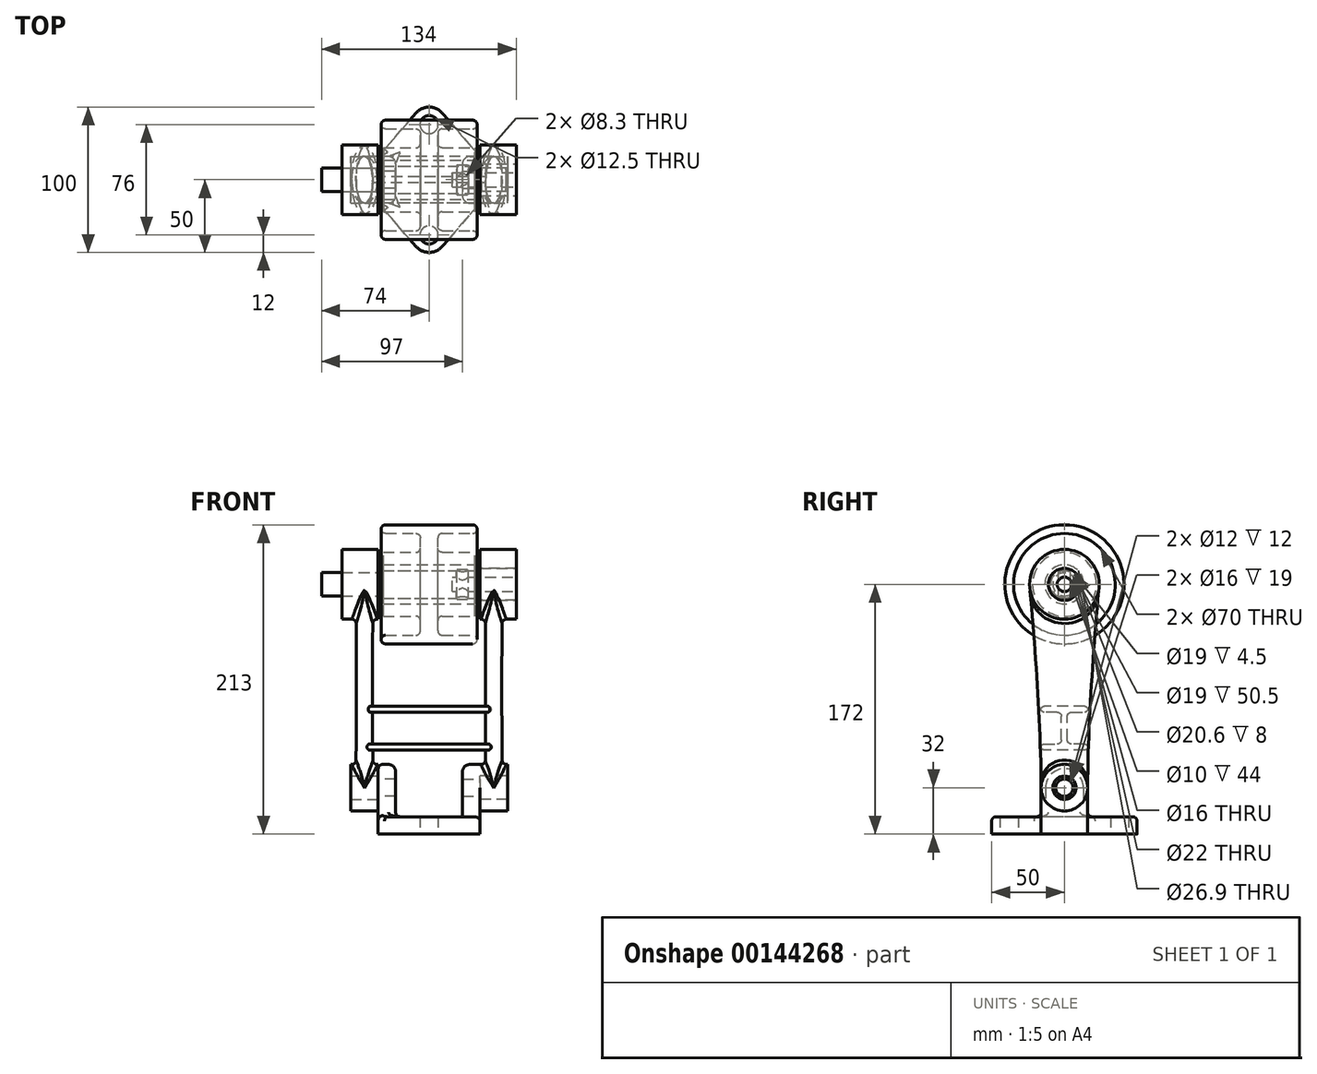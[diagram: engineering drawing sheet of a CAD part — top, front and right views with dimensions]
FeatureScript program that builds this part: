
annotation { "Feature Type Name" : "Feature", "Feature Type Description" : "" }
export const myFeature = defineFeature(function(context is Context, id is Id, definition is map)
    precondition{}
    {
        {
            var Q0;
            Q0=qCreatedBy(makeId("Top.planeOp"),FACE);
            var sketch = newSketch(context, id + "F0", { "sketchPlane" : qUnion([Q0])});
            skLineSegment(sketch, "E0", {"start": v(-9.06, -45.87) * mm, "end": v(-35, -16) * mm});
            skLineSegment(sketch, "E1", {"start": v(-35, 16) * mm, "end": v(-9.06, 45.87) * mm});
            skLineSegment(sketch, "E2", {"start": v(9.06, 45.87) * mm, "end": v(35, 16) * mm});
            skLineSegment(sketch, "E3", {"start": v(35, -16) * mm, "end": v(9.06, -45.87) * mm});
            skLineSegment(sketch, "E4", {"start": v(35, -16) * mm, "end": v(35, 16) * mm});
            skLineSegment(sketch, "E5", {"start": v(-35, -16) * mm, "end": v(-35, 16) * mm});
            skPoint(sketch, "E6.orphan", {"position": v(-48.9, 0) * mm});
            skPoint(sketch, "E7.orphan", {"position": v(48.9, 0) * mm});
            skPoint(sketch, "E8.visualSharp", {"position": v(0, -56.3) * mm});
            skArc(sketch, "E8.filletArc", {"start": v(-9.06, -45.87) * mm, "mid": v(0, -50) * mm, "end": v(9.06, -45.87) * mm});
            skPoint(sketch, "E9.visualSharp", {"position": v(0, 56.3) * mm});
            skArc(sketch, "E9.filletArc", {"start": v(9.06, 45.87) * mm, "mid": v(0, 50) * mm, "end": v(-9.06, 45.87) * mm});
            skCircle(sketch, "E10", {"center": v(0, -38) * mm, "radius": 6.25 * mm});
            skCircle(sketch, "E11", {"center": v(0, 38) * mm, "radius": 6.25 * mm});
            skSolve(sketch);
        }
        {
            var Q0;
            Q0 = qSketchRegion(id + "F0", true);
            extrude(context, id + "F1", {"entities" : qUnion([Q0]), "depth" : 12 * mm});
        }
        {
            var Q0;
            Q0=makeQuery(id+"F1.opExtrude","SWEPT_FACE",FACE,{"disambiguationData":[OSD([sQuery(id+"F0.wireOp",EDGE,"E5")])]});
            var sketch = newSketch(context, id + "F2", { "sketchPlane" : qUnion([Q0])});
            skLineSegment(sketch, "E12", {"start": v(-16, 0) * mm, "end": v(-16, 32) * mm});
            skLineSegment(sketch, "E13", {"start": v(16, 0) * mm, "end": v(16, 32) * mm});
            skArc(sketch, "E14", {"start": v(16, 32) * mm, "mid": v(0, 48) * mm, "end": v(-16, 32) * mm});
            skLineSegment(sketch, "E15", {"start": v(-16, 0) * mm, "end": v(16, 0) * mm});
            skCircle(sketch, "E16", {"center": v(0, 32) * mm, "radius": 6 * mm});
            skSolve(sketch);
        }
        {
            var Q0;
            Q0 = qSketchRegion(id + "F2", true);
            extrude(context, id + "F3", {"entities" : qUnion([Q0]), "operationType" : NewBodyOperationType.ADD, "oppositeDirection" : true, "depth" : 12 * mm});
        }
        {
            var Q0;
            Q0=makeQuery(id+"F1.opExtrude","SWEPT_BODY",BODY,{"disambiguationData":[OSD([sQuery(id+"F0.wireOp",EDGE,"E0"),sQuery(id+"F0.wireOp",EDGE,"E1"),sQuery(id+"F0.wireOp",EDGE,"E2"),sQuery(id+"F0.wireOp",EDGE,"E3"),sQuery(id+"F0.wireOp",EDGE,"E4"),sQuery(id+"F0.wireOp",EDGE,"E5"),sQuery(id+"F0.wireOp",EDGE,"E8.filletArc"),sQuery(id+"F0.wireOp",EDGE,"E9.filletArc"),sQuery(id+"F0.wireOp",EDGE,"E10"),sQuery(id+"F0.wireOp",EDGE,"E11")])]});
            var Q1;
            Q1=qCreatedBy(makeId("Right.planeOp"),FACE);
            mirror(context, id + "F4", {"operationType" : NewBodyOperationType.ADD, "entities" : qUnion([Q0]), "mirrorPlane" : qUnion([Q1])});
        }
        {
            var Q0;
            Q0=makeQuery(id+"F4.opPattern","COPY",EDGE,{"derivedFrom":makeQuery(id+"F3.boolean.opBoolean","INTERSECT",EDGE,{"derivedFrom":[makeQuery(id+"F1.opExtrude","CAP_FACE",FACE,{"disambiguationData":[OSD([sQuery(id+"F0.wireOp",EDGE,"E0"),sQuery(id+"F0.wireOp",EDGE,"E1"),sQuery(id+"F0.wireOp",EDGE,"E2"),sQuery(id+"F0.wireOp",EDGE,"E3"),sQuery(id+"F0.wireOp",EDGE,"E4"),sQuery(id+"F0.wireOp",EDGE,"E5"),sQuery(id+"F0.wireOp",EDGE,"E8.filletArc"),sQuery(id+"F0.wireOp",EDGE,"E9.filletArc"),sQuery(id+"F0.wireOp",EDGE,"E10"),sQuery(id+"F0.wireOp",EDGE,"E11")])],"isStart":false}),makeQuery(id+"F3.opExtrude","SWEPT_FACE",FACE,{"disambiguationData":[OSD([sQuery(id+"F2.wireOp",EDGE,"E12")])]})]}),"instanceName":"1"});
            var Q1;
            Q1=makeQuery(id+"F4.opPattern","COPY",EDGE,{"derivedFrom":makeQuery(id+"F3.boolean.opBoolean","INTERSECT",EDGE,{"derivedFrom":[makeQuery(id+"F1.opExtrude","CAP_FACE",FACE,{"disambiguationData":[OSD([sQuery(id+"F0.wireOp",EDGE,"E0"),sQuery(id+"F0.wireOp",EDGE,"E1"),sQuery(id+"F0.wireOp",EDGE,"E2"),sQuery(id+"F0.wireOp",EDGE,"E3"),sQuery(id+"F0.wireOp",EDGE,"E4"),sQuery(id+"F0.wireOp",EDGE,"E5"),sQuery(id+"F0.wireOp",EDGE,"E8.filletArc"),sQuery(id+"F0.wireOp",EDGE,"E9.filletArc"),sQuery(id+"F0.wireOp",EDGE,"E10"),sQuery(id+"F0.wireOp",EDGE,"E11")])],"isStart":false}),makeQuery(id+"F3.opExtrude","CAP_FACE",FACE,{"disambiguationData":[OSD([sQuery(id+"F2.wireOp",EDGE,"E12"),sQuery(id+"F2.wireOp",EDGE,"E13"),sQuery(id+"F2.wireOp",EDGE,"E14"),sQuery(id+"F2.wireOp",EDGE,"E15"),sQuery(id+"F2.wireOp",EDGE,"E16")])],"isStart":false})]}),"instanceName":"1"});
            var Q2;
            Q2=makeQuery(id+"F4.opPattern","COPY",EDGE,{"derivedFrom":makeQuery(id+"F3.boolean.opBoolean","INTERSECT",EDGE,{"derivedFrom":[makeQuery(id+"F1.opExtrude","CAP_FACE",FACE,{"disambiguationData":[OSD([sQuery(id+"F0.wireOp",EDGE,"E0"),sQuery(id+"F0.wireOp",EDGE,"E1"),sQuery(id+"F0.wireOp",EDGE,"E2"),sQuery(id+"F0.wireOp",EDGE,"E3"),sQuery(id+"F0.wireOp",EDGE,"E4"),sQuery(id+"F0.wireOp",EDGE,"E5"),sQuery(id+"F0.wireOp",EDGE,"E8.filletArc"),sQuery(id+"F0.wireOp",EDGE,"E9.filletArc"),sQuery(id+"F0.wireOp",EDGE,"E10"),sQuery(id+"F0.wireOp",EDGE,"E11")])],"isStart":false}),makeQuery(id+"F3.opExtrude","SWEPT_FACE",FACE,{"disambiguationData":[OSD([sQuery(id+"F2.wireOp",EDGE,"E13")])]})]}),"instanceName":"1"});
            var Q3;
            Q3=makeQuery(id+"F3.boolean.opBoolean","INTERSECT",EDGE,{"derivedFrom":[makeQuery(id+"F1.opExtrude","CAP_FACE",FACE,{"disambiguationData":[OSD([sQuery(id+"F0.wireOp",EDGE,"E0"),sQuery(id+"F0.wireOp",EDGE,"E1"),sQuery(id+"F0.wireOp",EDGE,"E2"),sQuery(id+"F0.wireOp",EDGE,"E3"),sQuery(id+"F0.wireOp",EDGE,"E4"),sQuery(id+"F0.wireOp",EDGE,"E5"),sQuery(id+"F0.wireOp",EDGE,"E8.filletArc"),sQuery(id+"F0.wireOp",EDGE,"E9.filletArc"),sQuery(id+"F0.wireOp",EDGE,"E10"),sQuery(id+"F0.wireOp",EDGE,"E11")])],"isStart":false}),makeQuery(id+"F3.opExtrude","SWEPT_FACE",FACE,{"disambiguationData":[OSD([sQuery(id+"F2.wireOp",EDGE,"E13")])]})]});
            var Q4;
            Q4=makeQuery(id+"F3.boolean.opBoolean","INTERSECT",EDGE,{"derivedFrom":[makeQuery(id+"F1.opExtrude","CAP_FACE",FACE,{"disambiguationData":[OSD([sQuery(id+"F0.wireOp",EDGE,"E0"),sQuery(id+"F0.wireOp",EDGE,"E1"),sQuery(id+"F0.wireOp",EDGE,"E2"),sQuery(id+"F0.wireOp",EDGE,"E3"),sQuery(id+"F0.wireOp",EDGE,"E4"),sQuery(id+"F0.wireOp",EDGE,"E5"),sQuery(id+"F0.wireOp",EDGE,"E8.filletArc"),sQuery(id+"F0.wireOp",EDGE,"E9.filletArc"),sQuery(id+"F0.wireOp",EDGE,"E10"),sQuery(id+"F0.wireOp",EDGE,"E11")])],"isStart":false}),makeQuery(id+"F3.opExtrude","CAP_FACE",FACE,{"disambiguationData":[OSD([sQuery(id+"F2.wireOp",EDGE,"E12"),sQuery(id+"F2.wireOp",EDGE,"E13"),sQuery(id+"F2.wireOp",EDGE,"E14"),sQuery(id+"F2.wireOp",EDGE,"E15"),sQuery(id+"F2.wireOp",EDGE,"E16")])],"isStart":false})]});
            var Q5;
            Q5=makeQuery(id+"F3.boolean.opBoolean","INTERSECT",EDGE,{"derivedFrom":[makeQuery(id+"F1.opExtrude","CAP_FACE",FACE,{"disambiguationData":[OSD([sQuery(id+"F0.wireOp",EDGE,"E0"),sQuery(id+"F0.wireOp",EDGE,"E1"),sQuery(id+"F0.wireOp",EDGE,"E2"),sQuery(id+"F0.wireOp",EDGE,"E3"),sQuery(id+"F0.wireOp",EDGE,"E4"),sQuery(id+"F0.wireOp",EDGE,"E5"),sQuery(id+"F0.wireOp",EDGE,"E8.filletArc"),sQuery(id+"F0.wireOp",EDGE,"E9.filletArc"),sQuery(id+"F0.wireOp",EDGE,"E10"),sQuery(id+"F0.wireOp",EDGE,"E11")])],"isStart":false}),makeQuery(id+"F3.opExtrude","SWEPT_FACE",FACE,{"disambiguationData":[OSD([sQuery(id+"F2.wireOp",EDGE,"E12")])]})]});
            fillet(context, id + "F5", {"entities" : qUnion([Q0, Q1, Q2, Q3, Q4, Q5]), "radius" : 3 * mm, "tangentPropagation" : true, "allowEdgeOverflow" : false});
        }
        {
            var Q0;
            Q0=makeQuery(id+"F1.opExtrude","CAP_EDGE",EDGE,{"disambiguationData":[OSD([sQuery(id+"F0.wireOp",EDGE,"E1")])],"isStart":false});
            var Q1;
            Q1=makeQuery(id+"F1.opExtrude","CAP_EDGE",EDGE,{"disambiguationData":[OSD([sQuery(id+"F0.wireOp",EDGE,"E0")])],"isStart":false});
            fillet(context, id + "F6", {"entities" : qUnion([Q0, Q1]), "radius" : 3 * mm, "tangentPropagation" : true, "allowEdgeOverflow" : false});
        }
        {
            var Q0;
            Q0=makeQuery(id+"F4.opPattern","COPY",EDGE,{"derivedFrom":makeQuery(id+"F3.opExtrude","CAP_EDGE",EDGE,{"disambiguationData":[OSD([sQuery(id+"F2.wireOp",EDGE,"E14")])],"isStart":false}),"instanceName":"1"});
            var Q1;
            Q1=makeQuery(id+"F3.opExtrude","CAP_EDGE",EDGE,{"disambiguationData":[OSD([sQuery(id+"F2.wireOp",EDGE,"E14")])],"isStart":false});
            fillet(context, id + "F7", {"entities" : qUnion([Q0, Q1]), "radius" : 5 * mm, "tangentPropagation" : true, "allowEdgeOverflow" : false});
        }
        {
            var Q0;
            Q0=makeQuery(id+"F4.boolean.opBoolean","MERGE",FACE,{"derivedFrom":[makeQuery(id+"F1.opExtrude","SWEPT_FACE",FACE,{"disambiguationData":[OSD([sQuery(id+"F0.wireOp",EDGE,"E4")])]}),makeQuery(id+"F4.opPattern","COPY",FACE,{"derivedFrom":makeQuery(id+"F3.boolean.opBoolean","MERGE",FACE,{"derivedFrom":[makeQuery(id+"F1.opExtrude","SWEPT_FACE",FACE,{"disambiguationData":[OSD([sQuery(id+"F0.wireOp",EDGE,"E5")])]}),makeQuery(id+"F3.opExtrude","CAP_FACE",FACE,{"disambiguationData":[OSD([sQuery(id+"F2.wireOp",EDGE,"E12"),sQuery(id+"F2.wireOp",EDGE,"E13"),sQuery(id+"F2.wireOp",EDGE,"E14"),sQuery(id+"F2.wireOp",EDGE,"E15"),sQuery(id+"F2.wireOp",EDGE,"E16")])],"isStart":true})]}),"instanceName":"1"})]});
            var sketch = newSketch(context, id + "F8", { "sketchPlane" : qUnion([Q0])});
            skCircle(sketch, "E17", {"center": v(0, 32) * mm, "radius": 8 * mm});
            skCircle(sketch, "E18", {"center": v(0, 32) * mm, "radius": 16 * mm});
            skSolve(sketch);
        }
        {
            var Q0;
            Q0 = qSketchRegion(id + "F8", true);
            extrude(context, id + "F9", {"entities" : qUnion([Q0]), "depth" : 19 * mm});
        }
        {
            var Q0;
            Q0=makeQuery(id+"F4.boolean.opBoolean","MERGE",FACE,{"derivedFrom":[makeQuery(id+"F1.opExtrude","SWEPT_FACE",FACE,{"disambiguationData":[OSD([sQuery(id+"F0.wireOp",EDGE,"E4")])]}),makeQuery(id+"F4.opPattern","COPY",FACE,{"derivedFrom":makeQuery(id+"F3.boolean.opBoolean","MERGE",FACE,{"derivedFrom":[makeQuery(id+"F1.opExtrude","SWEPT_FACE",FACE,{"disambiguationData":[OSD([sQuery(id+"F0.wireOp",EDGE,"E5")])]}),makeQuery(id+"F3.opExtrude","CAP_FACE",FACE,{"disambiguationData":[OSD([sQuery(id+"F2.wireOp",EDGE,"E12"),sQuery(id+"F2.wireOp",EDGE,"E13"),sQuery(id+"F2.wireOp",EDGE,"E14"),sQuery(id+"F2.wireOp",EDGE,"E15"),sQuery(id+"F2.wireOp",EDGE,"E16")])],"isStart":true})]}),"instanceName":"1"})]});
            var sketch = newSketch(context, id + "F10", { "sketchPlane" : qUnion([Q0])});
            skCircle(sketch, "E19", {"center": v(0, 172) * mm, "radius": 8 * mm});
            skCircle(sketch, "E20", {"center": v(0, 172) * mm, "radius": 24 * mm});
            skSolve(sketch);
        }
        {
            var Q0;
            Q0 = qSketchRegion(id + "F10", true);
            extrude(context, id + "F11", {"entities" : qUnion([Q0]), "depth" : 25 * mm});
        }
        {
            var Q0;
            Q0=qCreatedBy(makeId("Top.planeOp"),FACE);
            var Q1;
            Q1=sQuery(id+"F2.wireOp",VERTEX,"E14.center");
            cPlane(context, id + "F12", {"entities" : qUnion([Q0, Q1]), "cplaneType" : CPlaneType.PLANE_POINT, "offset" : 25 * mm, "width" : 150 * mm, "height" : 150 * mm});
        }
        {
            var Q0;
            Q0=qCreatedBy(id+"F12.planeOp",FACE);
            var sketch = newSketch(context, id + "F13", { "sketchPlane" : qUnion([Q0])});
            skEllipse(sketch, "E21", {"center": v(44.5, 0) * mm, "majorRadius": 16 * mm, "minorRadius": 6 * mm, "majorAxis": v(0, -1)});
            skSolve(sketch);
        }
        {
            var Q0;
            Q0=makeQuery(id+"F4.boolean.opBoolean","MERGE",FACE,{"derivedFrom":[makeQuery(id+"F1.opExtrude","SWEPT_FACE",FACE,{"disambiguationData":[OSD([sQuery(id+"F0.wireOp",EDGE,"E4")])]}),makeQuery(id+"F4.opPattern","COPY",FACE,{"derivedFrom":makeQuery(id+"F3.boolean.opBoolean","MERGE",FACE,{"derivedFrom":[makeQuery(id+"F1.opExtrude","SWEPT_FACE",FACE,{"disambiguationData":[OSD([sQuery(id+"F0.wireOp",EDGE,"E5")])]}),makeQuery(id+"F3.opExtrude","CAP_FACE",FACE,{"disambiguationData":[OSD([sQuery(id+"F2.wireOp",EDGE,"E12"),sQuery(id+"F2.wireOp",EDGE,"E13"),sQuery(id+"F2.wireOp",EDGE,"E14"),sQuery(id+"F2.wireOp",EDGE,"E15"),sQuery(id+"F2.wireOp",EDGE,"E16")])],"isStart":true})]}),"instanceName":"1"})]});
            var sketch = newSketch(context, id + "F14", { "sketchPlane" : qUnion([Q0])});
            skCircle(sketch, "E22.0", {"center": v(0, 32) * mm, "radius": 8 * mm});
            skSolve(sketch);
        }
        {
            var Q0;
            Q0=makeQuery(id+"F14.imprint","IMPRINT",FACE,{"disambiguationData":[TD([[makeQuery(id+"F14.imprint","IMPRINT",EDGE,{"derivedFrom":sQuery(id+"F14.wireOp",EDGE,"E22.0")}),-1.0]])]});
            var sketch = newSketch(context, id + "F15", { "sketchPlane" : qUnion([Q0])});
            skCircle(sketch, "E23.0", {"center": v(0, 32) * mm, "radius": 8 * mm});
            skSolve(sketch);
        }
        {
            var Q0;
            Q0 = qSketchRegion(id + "F15", true);
            extrude(context, id + "F16", {"entities" : qUnion([Q0]), "operationType" : NewBodyOperationType.REMOVE, "depth" : 25 * mm});
        }
        {
            var Q0;
            Q0=qCreatedBy(id+"F12.planeOp",FACE);
            var Q1;
            Q1=sQuery(id+"F10.wireOp",VERTEX,"E19.center");
            cPlane(context, id + "F17", {"entities" : qUnion([Q0, Q1]), "cplaneType" : CPlaneType.PLANE_POINT, "offset" : 25 * mm, "width" : 150 * mm, "height" : 150 * mm});
        }
        {
            var Q0;
            Q0=qCreatedBy(id+"F17.planeOp",FACE);
            var sketch = newSketch(context, id + "F18", { "sketchPlane" : qUnion([Q0])});
            skEllipse(sketch, "E24", {"center": v(44.5, 0) * mm, "majorRadius": 24 * mm, "minorRadius": 6 * mm, "majorAxis": v(0, 1)});
            skSolve(sketch);
        }
        {
            var Q0;
            Q0 = qSketchRegion(id + "F13", true);
            var Q1;
            Q1 = qSketchRegion(id + "F18", true);
            loft(context, id + "F19", {"operationType" : NewBodyOperationType.ADD, "sheetProfilesArray" : [{ "sheetProfileEntities" : qUnion([Q0]) }, { "sheetProfileEntities" : qUnion([Q1]) }]});
        }
        {
            var Q0;
            Q0=makeQuery(id+"F11.opExtrude","CAP_FACE",FACE,{"disambiguationData":[OSD([sQuery(id+"F10.wireOp",EDGE,"E19"),sQuery(id+"F10.wireOp",EDGE,"E20")])],"isStart":false});
            var sketch = newSketch(context, id + "F20", { "sketchPlane" : qUnion([Q0])});
            skCircle(sketch, "E25.0", {"center": v(0, 172) * mm, "radius": 8 * mm});
            skSolve(sketch);
        }
        {
            var Q0;
            Q0 = qSketchRegion(id + "F20", true);
            extrude(context, id + "F21", {"entities" : qUnion([Q0]), "operationType" : NewBodyOperationType.REMOVE, "endBound" : BoundingType.THROUGH_ALL, "oppositeDirection" : true, "depth" : 25 * mm});
        }
        {
            var Q0;
            Q0=makeQuery(id+"F9.opExtrude","CAP_FACE",FACE,{"disambiguationData":[OSD([sQuery(id+"F8.wireOp",EDGE,"E17"),sQuery(id+"F8.wireOp",EDGE,"E18")])],"isStart":true});
            var sketch = newSketch(context, id + "F22", { "sketchPlane" : qUnion([Q0])});
            skCircle(sketch, "E26.0", {"center": v(0, 32) * mm, "radius": 8 * mm});
            skSolve(sketch);
        }
        {
            var Q0;
            Q0 = qSketchRegion(id + "F22", true);
            extrude(context, id + "F23", {"entities" : qUnion([Q0]), "operationType" : NewBodyOperationType.REMOVE, "oppositeDirection" : true, "depth" : 25 * mm});
        }
        {
            var Q0;
            Q0=qCreatedBy(makeId("Right.planeOp"),FACE);
            var sketch = newSketch(context, id + "F24", { "sketchPlane" : qUnion([Q0])});
            skLineSegment(sketch, "E27", {"start": v(0, 88) * mm, "end": v(14, 88) * mm});
            skLineSegment(sketch, "E28", {"start": v(14, 84) * mm, "end": v(5, 84) * mm});
            skLineSegment(sketch, "E29", {"start": v(2, 81) * mm, "end": v(2, 65) * mm});
            skLineSegment(sketch, "E30", {"start": v(5, 62) * mm, "end": v(14, 62) * mm});
            skLineSegment(sketch, "E31", {"start": v(14, 58) * mm, "end": v(0, 58) * mm});
            skArc(sketch, "E32", {"start": v(14, 84) * mm, "mid": v(16, 86) * mm, "end": v(14, 88) * mm});
            skArc(sketch, "E33", {"start": v(14, 58) * mm, "mid": v(16, 60) * mm, "end": v(14, 62) * mm});
            skPoint(sketch, "E34.visualSharp", {"position": v(2, 84) * mm});
            skArc(sketch, "E34.filletArc", {"start": v(5, 84) * mm, "mid": v(2.88, 83.12) * mm, "end": v(2, 81) * mm});
            skPoint(sketch, "E35.visualSharp", {"position": v(2, 62) * mm});
            skArc(sketch, "E35.filletArc", {"start": v(2, 65) * mm, "mid": v(2.88, 62.88) * mm, "end": v(5, 62) * mm});
            skPoint(sketch, "E36.visualSharp", {"position": v(-2, 62) * mm});
            skPoint(sketch, "E37.visualSharp", {"position": v(-2, 84) * mm});
            skLineSegment(sketch, "E38", {"start": v(0, 32) * mm, "end": v(0, 94.51) * mm, "construction": true});
            skPoint(sketch, "E39.start.orphan", {"position": v(-16, 88) * mm});
            skPoint(sketch, "E40.end.orphan", {"position": v(-16, 84) * mm});
            skPoint(sketch, "E41.end.orphan", {"position": v(-16, 58) * mm});
            skPoint(sketch, "E41.start.orphan", {"position": v(-16, 62) * mm});
            skArc(sketch, "E42.MirrorCS", {"start": v(-2, 65) * mm, "mid": v(-2.88, 62.88) * mm, "end": v(-5, 62) * mm});
            skArc(sketch, "E43.MirrorCS", {"start": v(-5, 84) * mm, "mid": v(-2.88, 83.12) * mm, "end": v(-2, 81) * mm});
            skPoint(sketch, "E44.MirrorP", {"position": v(16, 84) * mm});
            skArc(sketch, "E45.MirrorCS", {"start": v(-14, 84) * mm, "mid": v(-16, 86) * mm, "end": v(-14, 88) * mm});
            skArc(sketch, "E46.MirrorCS", {"start": v(-14, 58) * mm, "mid": v(-16, 60) * mm, "end": v(-14, 62) * mm});
            skLineSegment(sketch, "E47.MirrorCS", {"start": v(-14, 58) * mm, "end": v(0, 58) * mm});
            skLineSegment(sketch, "E48.MirrorCS", {"start": v(0, 88) * mm, "end": v(-14, 88) * mm});
            skLineSegment(sketch, "E49.MirrorCS", {"start": v(-5, 62) * mm, "end": v(-14, 62) * mm});
            skPoint(sketch, "E50.MirrorP", {"position": v(16, 62) * mm});
            skPoint(sketch, "E51.MirrorP", {"position": v(16, 88) * mm});
            skLineSegment(sketch, "E52.MirrorCS", {"start": v(-2, 81) * mm, "end": v(-2, 65) * mm});
            skLineSegment(sketch, "E53.MirrorCS", {"start": v(-14, 84) * mm, "end": v(-5, 84) * mm});
            skPoint(sketch, "E54.MirrorP", {"position": v(16, 58) * mm});
            skSolve(sketch);
        }
        {
            var Q0;
            Q0 = qSketchRegion(id + "F24", true);
            extrude(context, id + "F25", {"entities" : qUnion([Q0]), "operationType" : NewBodyOperationType.ADD, "endBound" : BoundingType.UP_TO_NEXT, "depth" : 25 * mm});
        }
        {
            var Q0;
            Q0=makeQuery(id+"F19.boolean.opBoolean","INTERSECT",EDGE,{"derivedFrom":[makeQuery(id+"F9.opExtrude","SWEPT_FACE",FACE,{"disambiguationData":[OSD([sQuery(id+"F8.wireOp",EDGE,"E18")])]}),makeQuery(id+"F19.opLoft","SWEPT_FACE",FACE,{"disambiguationData":[OSD([sQuery(id+"F13.wireOp",EDGE,"E21"),sQuery(id+"F18.wireOp",EDGE,"E24")])]})]});
            var Q1;
            Q1=makeQuery(id+"F25.opExtrude","CAP_EDGE",EDGE,{"disambiguationData":[OSD([sQuery(id+"F24.wireOp",EDGE,"E27"),sQuery(id+"F24.wireOp",EDGE,"E48.MirrorCS")])],"isStart":false});
            var Q2;
            Q2=makeQuery(id+"F19.boolean.opBoolean","INTERSECT",EDGE,{"derivedFrom":[makeQuery(id+"F11.opExtrude","SWEPT_FACE",FACE,{"disambiguationData":[OSD([sQuery(id+"F10.wireOp",EDGE,"E20")])]}),makeQuery(id+"F19.opLoft","SWEPT_FACE",FACE,{"disambiguationData":[OSD([sQuery(id+"F13.wireOp",EDGE,"E21"),sQuery(id+"F18.wireOp",EDGE,"E24")])]})]});
            fillet(context, id + "F26", {"entities" : qUnion([Q0, Q1, Q2]), "radius" : 3 * mm, "tangentPropagation" : true, "allowEdgeOverflow" : false});
        }
        {
            var Q0;
            Q0=makeQuery(id+"F9.opExtrude","SWEPT_BODY",BODY,{"disambiguationData":[OSD([sQuery(id+"F8.wireOp",EDGE,"E17"),sQuery(id+"F8.wireOp",EDGE,"E18")])]});
            var Q1;
            Q1=qCreatedBy(makeId("Right.planeOp"),FACE);
            mirror(context, id + "F27", {"operationType" : NewBodyOperationType.ADD, "entities" : qUnion([Q0]), "mirrorPlane" : qUnion([Q1])});
        }
        {
            var Q0;
            Q0=makeQuery(id+"F11.opExtrude","CAP_FACE",FACE,{"disambiguationData":[OSD([sQuery(id+"F10.wireOp",EDGE,"E19"),sQuery(id+"F10.wireOp",EDGE,"E20")])],"isStart":true});
            var sketch = newSketch(context, id + "F28", { "sketchPlane" : qUnion([Q0])});
            skCircle(sketch, "E55", {"center": v(0, 172) * mm, "radius": 11 * mm});
            skSolve(sketch);
        }
        {
            var Q0;
            Q0 = qSketchRegion(id + "F28", true);
            extrude(context, id + "F29", {"entities" : qUnion([Q0]), "operationType" : NewBodyOperationType.REMOVE, "oppositeDirection" : true, "depth" : 25 * mm});
        }
        {
            var Q0;
            Q0=qCreatedBy(makeId("Front.planeOp"),FACE);
            var sketch = newSketch(context, id + "F30", { "sketchPlane" : qUnion([Q0])});
            skLineSegment(sketch, "E56", {"start": v(-70, 172) * mm, "end": v(107.27, 172) * mm, "construction": true});
            skLineSegment(sketch, "E57", {"start": v(-31.5, 158.55) * mm, "end": v(-31.5, 150) * mm});
            skLineSegment(sketch, "E58", {"start": v(-31.5, 150) * mm, "end": v(-9, 150) * mm});
            skLineSegment(sketch, "E59", {"start": v(-6, 147) * mm, "end": v(-6, 140) * mm});
            skLineSegment(sketch, "E60", {"start": v(-9, 137) * mm, "end": v(-30, 137) * mm});
            skLineSegment(sketch, "E61", {"start": v(-30, 131) * mm, "end": v(0, 131) * mm});
            skArc(sketch, "E62", {"start": v(-30, 137) * mm, "mid": v(-33, 134) * mm, "end": v(-30, 131) * mm});
            skLineSegment(sketch, "E63", {"start": v(0, 122.2) * mm, "end": v(0, 204.02) * mm, "construction": true});
            skLineSegment(sketch, "E64", {"start": v(-31.5, 158.55) * mm, "end": v(0, 158.55) * mm});
            skPoint(sketch, "E65.visualSharp", {"position": v(-6, 150) * mm});
            skArc(sketch, "E65.filletArc", {"start": v(-6, 147) * mm, "mid": v(-6.88, 149.12) * mm, "end": v(-9, 150) * mm});
            skPoint(sketch, "E66.visualSharp", {"position": v(-6, 137) * mm});
            skArc(sketch, "E66.filletArc", {"start": v(-9, 137) * mm, "mid": v(-6.88, 137.88) * mm, "end": v(-6, 140) * mm});
            skArc(sketch, "E67.MirrorCS", {"start": v(9, 137) * mm, "mid": v(6.88, 137.88) * mm, "end": v(6, 140) * mm});
            skArc(sketch, "E68.MirrorCS", {"start": v(6, 147) * mm, "mid": v(6.88, 149.12) * mm, "end": v(9, 150) * mm});
            skLineSegment(sketch, "E69.MirrorCS", {"start": v(6, 147) * mm, "end": v(6, 140) * mm});
            skArc(sketch, "E70.MirrorCS", {"start": v(30, 137) * mm, "mid": v(33, 134) * mm, "end": v(30, 131) * mm});
            skLineSegment(sketch, "E71.MirrorCS", {"start": v(31.5, 158.55) * mm, "end": v(31.5, 150) * mm});
            skPoint(sketch, "E72.MirrorP", {"position": v(6, 137) * mm});
            skPoint(sketch, "E73.MirrorP", {"position": v(6, 150) * mm});
            skLineSegment(sketch, "E74.MirrorCS", {"start": v(30, 131) * mm, "end": v(0, 131) * mm});
            skLineSegment(sketch, "E75.MirrorCS", {"start": v(9, 137) * mm, "end": v(30, 137) * mm});
            skLineSegment(sketch, "E76.MirrorCS", {"start": v(31.5, 158.55) * mm, "end": v(0, 158.55) * mm});
            skLineSegment(sketch, "E77.MirrorCS", {"start": v(31.5, 150) * mm, "end": v(9, 150) * mm});
            skLineSegment(sketch, "E78.MirrorCS", {"start": v(70, 172) * mm, "end": v(-107.27, 172) * mm, "construction": true});
            skSolve(sketch);
        }
        {
            var Q0;
            Q0 = qSketchRegion(id + "F30", true);
            var Q1;
            Q1=sQuery(id+"F30.wireOp",EDGE,"E78.MirrorCS");
            revolve(context, id + "F31", {"entities" : qUnion([Q0]), "axis" : qUnion([Q1]), "revolveType" : RevolveType.FULL});
        }
        {
            var Q0;
            Q0=qCreatedBy(makeId("Front.planeOp"),FACE);
            var sketch = newSketch(context, id + "F32", { "sketchPlane" : qUnion([Q0])});
            skLineSegment(sketch, "E79.0", {"start": v(70, 172) * mm, "end": v(-107.27, 172) * mm, "construction": true});
            skLineSegment(sketch, "E80", {"start": v(60, 172) * mm, "end": v(60, 183) * mm});
            skLineSegment(sketch, "E81", {"start": v(60, 183) * mm, "end": v(35, 183) * mm});
            skLineSegment(sketch, "E82", {"start": v(35, 183) * mm, "end": v(35, 181.5) * mm});
            skLineSegment(sketch, "E83", {"start": v(35, 181.5) * mm, "end": v(-35, 181.5) * mm});
            skLineSegment(sketch, "E84", {"start": v(-35, 181.5) * mm, "end": v(-35, 180) * mm});
            skLineSegment(sketch, "E85", {"start": v(-74, 180) * mm, "end": v(-74, 172) * mm});
            skLineSegment(sketch, "E86", {"start": v(-74, 172) * mm, "end": v(60, 172) * mm});
            skLineSegment(sketch, "E87", {"start": v(-74, 180) * mm, "end": v(-35, 180) * mm});
            skSolve(sketch);
        }
        {
            var Q0;
            Q0 = qSketchRegion(id + "F32", true);
            var Q1;
            Q1=sQuery(id+"F32.wireOp",EDGE,"E79.0");
            revolve(context, id + "F33", {"entities" : qUnion([Q0]), "axis" : qUnion([Q1]), "revolveType" : RevolveType.FULL});
        }
        {
            var Q0;
            Q0=qCreatedBy(id+"F17.planeOp",FACE);
            var sketch = newSketch(context, id + "F34", { "sketchPlane" : qUnion([Q0])});
            skCircle(sketch, "E88", {"center": v(23, 0) * mm, "radius": 4.15 * mm});
            skSolve(sketch);
        }
        {
            var Q0;
            Q0 = qSketchRegion(id + "F34", true);
            var Q1;
            Q1=makeQuery(id+"F33.opRevolve","SWEPT_FACE",FACE,{"disambiguationData":[OSD([sQuery(id+"F32.wireOp",EDGE,"E83")])]});
            var Q2;
            Q2=makeQuery(id+"F33.opRevolve","SWEPT_FACE",FACE,{"disambiguationData":[OSD([sQuery(id+"F32.wireOp",EDGE,"E83")])]});
            extrude(context, id + "F35", {"entities" : qUnion([Q0]), "operationType" : NewBodyOperationType.REMOVE, "endBound" : BoundingType.UP_TO_SURFACE, "oppositeDirection" : true, "endBoundEntityFace" : qUnion([Q1]), "depth" : 25 * mm, "hasSecondDirection" : true, "secondDirectionBound" : SecondDirectionBoundingType.UP_TO_SURFACE, "secondDirectionOppositeDirection" : false, "secondDirectionBoundEntityFace" : qUnion([Q2]), "secondDirectionDepth" : 25 * mm});
        }
        {
            var Q0;
            Q0=makeQuery(id+"F33.opRevolve","SWEPT_FACE",FACE,{"disambiguationData":[OSD([sQuery(id+"F32.wireOp",EDGE,"E80")])]});
            var sketch = newSketch(context, id + "F36", { "sketchPlane" : qUnion([Q0])});
            skCircle(sketch, "E89", {"center": v(0, 172) * mm, "radius": 5 * mm});
            skSolve(sketch);
        }
        {
            var Q0;
            Q0 = qSketchRegion(id + "F36", true);
            extrude(context, id + "F37", {"entities" : qUnion([Q0]), "operationType" : NewBodyOperationType.REMOVE, "oppositeDirection" : true, "depth" : 44 * mm});
        }
        {
            var Q0;
            Q0=qCreatedBy(makeId("Front.planeOp"),FACE);
            var sketch = newSketch(context, id + "F38", { "sketchPlane" : qUnion([Q0])});
            skLineSegment(sketch, "E90", {"start": v(72.55, 172) * mm, "end": v(-85.73, 172) * mm, "construction": true});
            skLineSegment(sketch, "E91", {"start": v(-31.5, 185.45) * mm, "end": v(-31.5, 181.5) * mm});
            skLineSegment(sketch, "E92", {"start": v(27, 182.3) * mm, "end": v(27, 181.5) * mm});
            skLineSegment(sketch, "E93", {"start": v(31.5, 181.5) * mm, "end": v(31.5, 185.45) * mm});
            skLineSegment(sketch, "E94", {"start": v(31.5, 185.45) * mm, "end": v(-31.5, 185.45) * mm});
            skLineSegment(sketch, "E95", {"start": v(27, 181.5) * mm, "end": v(31.5, 181.5) * mm});
            skLineSegment(sketch, "E96", {"start": v(27, 182.3) * mm, "end": v(19, 182.3) * mm});
            skLineSegment(sketch, "E97", {"start": v(19, 182.3) * mm, "end": v(19, 181.5) * mm});
            skLineSegment(sketch, "E98", {"start": v(19, 181.5) * mm, "end": v(-31.5, 181.5) * mm});
            skSolve(sketch);
        }
        {
            var Q0;
            Q0 = qSketchRegion(id + "F38", true);
            var Q1;
            Q1=sQuery(id+"F38.wireOp",EDGE,"E90");
            revolve(context, id + "F39", {"entities" : qUnion([Q0]), "axis" : qUnion([Q1]), "revolveType" : RevolveType.FULL});
        }
    });
